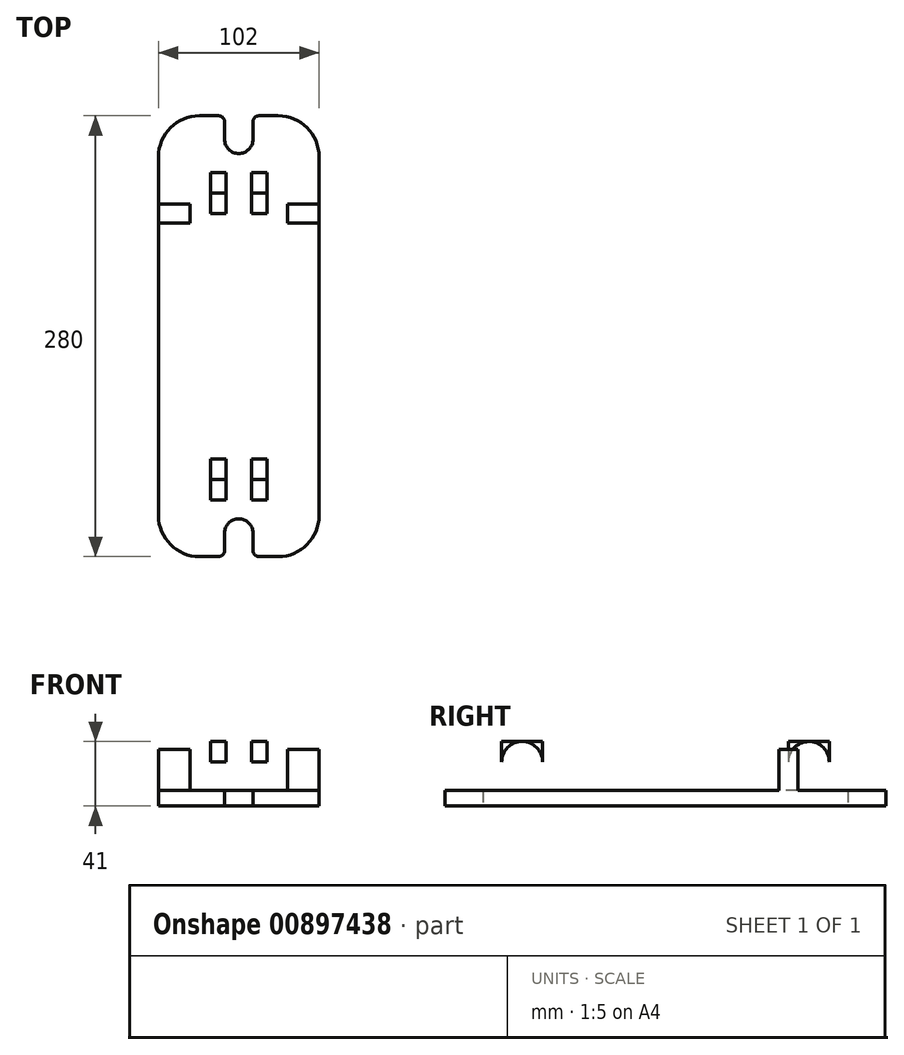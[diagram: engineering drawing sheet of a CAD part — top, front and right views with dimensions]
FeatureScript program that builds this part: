
annotation { "Feature Type Name" : "Feature", "Feature Type Description" : "" }
export const myFeature = defineFeature(function(context is Context, id is Id, definition is map)
    precondition{}
    {
        {
            var Q0;
            Q0=qCreatedBy(makeId("Top.planeOp"),FACE);
            var sketch = newSketch(context, id + "F0", { "sketchPlane" : qUnion([Q0])});
            skLineSegment(sketch, "E0.bottom", {"start": v(-25, 140) * mm, "end": v(-9, 140) * mm});
            skLineSegment(sketch, "E0.top", {"start": v(-25, -140) * mm, "end": v(-9, -140) * mm});
            skLineSegment(sketch, "E0.left", {"start": v(-51, 114) * mm, "end": v(-51, -114) * mm});
            skLineSegment(sketch, "E0.right", {"start": v(51, 114) * mm, "end": v(51, -114) * mm});
            skPoint(sketch, "E0.middle", {"position": v(0, 0) * mm});
            skLineSegment(sketch, "E1", {"start": v(9, -140) * mm, "end": v(9, -125) * mm});
            skPoint(sketch, "E2.startSnap0", {"position": v(0, -140) * mm});
            skLineSegment(sketch, "E3", {"start": v(0, -87.37) * mm, "end": v(0, 88.05) * mm, "construction": true});
            skLineSegment(sketch, "E4", {"start": v(90.42, 0) * mm, "end": v(-89.23, 0) * mm, "construction": true});
            skPoint(sketch, "E4.startSnap0", {"position": v(51, 0) * mm});
            skLineSegment(sketch, "E5.MirrorCS", {"start": v(-9, -140) * mm, "end": v(-9, -125) * mm});
            skPoint(sketch, "E6.MirrorCS.end.orphan", {"position": v(-9, -116) * mm});
            skLineSegment(sketch, "E7", {"start": v(0, -116) * mm, "end": v(0, -116) * mm});
            skPoint(sketch, "E8.visualSharp", {"position": v(9, -116) * mm});
            skArc(sketch, "E8.filletArc", {"start": v(9, -125) * mm, "mid": v(6.36, -118.64) * mm, "end": v(0, -116) * mm});
            skArc(sketch, "E9.filletArc", {"start": v(0, -116) * mm, "mid": v(-6.36, -118.64) * mm, "end": v(-9, -125) * mm});
            skLineSegment(sketch, "E10.trimOffspring", {"start": v(9, -140) * mm, "end": v(25, -140) * mm});
            skLineSegment(sketch, "E11.MirrorCS", {"start": v(9, 140) * mm, "end": v(9, 125) * mm});
            skArc(sketch, "E12.MirrorCS", {"start": v(9, 125) * mm, "mid": v(6.36, 118.64) * mm, "end": v(0, 116) * mm});
            skArc(sketch, "E13.MirrorCS", {"start": v(0, 116) * mm, "mid": v(-6.36, 118.64) * mm, "end": v(-9, 125) * mm});
            skLineSegment(sketch, "E14.MirrorCS", {"start": v(-9, 140) * mm, "end": v(-9, 125) * mm});
            skLineSegment(sketch, "E15.trimOffspring", {"start": v(9, 140) * mm, "end": v(25, 140) * mm});
            skPoint(sketch, "E16.visualSharp", {"position": v(51, 140) * mm});
            skArc(sketch, "E16.filletArc", {"start": v(51, 114) * mm, "mid": v(43.38, 132.38) * mm, "end": v(25, 140) * mm});
            skPoint(sketch, "E17.visualSharp", {"position": v(-51, 140) * mm});
            skArc(sketch, "E17.filletArc", {"start": v(-25, 140) * mm, "mid": v(-43.38, 132.38) * mm, "end": v(-51, 114) * mm});
            skPoint(sketch, "E18.visualSharp", {"position": v(-51, -140) * mm});
            skArc(sketch, "E18.filletArc", {"start": v(-51, -114) * mm, "mid": v(-43.38, -132.38) * mm, "end": v(-25, -140) * mm});
            skPoint(sketch, "E19.visualSharp", {"position": v(51, -140) * mm});
            skArc(sketch, "E19.filletArc", {"start": v(25, -140) * mm, "mid": v(43.38, -132.38) * mm, "end": v(51, -114) * mm});
            skSolve(sketch);
        }
        {
            var Q0;
            Q0=makeQuery(id+"F0.imprint","IMPRINT",FACE,{"disambiguationData":[TD([[makeQuery(id+"F0.imprint","IMPRINT",EDGE,{"derivedFrom":sQuery(id+"F0.wireOp",EDGE,"E0.bottom")}),-1.0]])]});
            extrude(context, id + "F1", {"entities" : qUnion([Q0]), "depth" : 10 * mm, "offsetDistance" : 25 * mm});
        }
        {
            var Q0;
            Q0=makeQuery(id+"F1.opExtrude","SWEPT_EDGE",EDGE,{"disambiguationData":[OSD([sQuery(id+"F0.wireOp",EDGE,"E0.top"),sQuery(id+"F0.wireOp",EDGE,"E5.MirrorCS")])]});
            var Q1;
            Q1=makeQuery(id+"F1.opExtrude","SWEPT_EDGE",EDGE,{"disambiguationData":[OSD([sQuery(id+"F0.wireOp",EDGE,"E1"),sQuery(id+"F0.wireOp",EDGE,"E10.trimOffspring")])]});
            var Q2;
            Q2=makeQuery(id+"F1.opExtrude","SWEPT_EDGE",EDGE,{"disambiguationData":[OSD([sQuery(id+"F0.wireOp",EDGE,"E0.bottom"),sQuery(id+"F0.wireOp",EDGE,"E14.MirrorCS")])]});
            var Q3;
            Q3=makeQuery(id+"F1.opExtrude","SWEPT_EDGE",EDGE,{"disambiguationData":[OSD([sQuery(id+"F0.wireOp",EDGE,"E11.MirrorCS"),sQuery(id+"F0.wireOp",EDGE,"E15.trimOffspring")])]});
            fillet(context, id + "F2", {"entities" : qUnion([Q0, Q1, Q2, Q3]), "radius" : 4 * mm, "tangentPropagation" : true, "allowEdgeOverflow" : false});
        }
        {
            var Q0;
            Q0=makeQuery(id+"F1.opExtrude","CAP_FACE",FACE,{"disambiguationData":[OSD([sQuery(id+"F0.wireOp",EDGE,"E0.bottom"),sQuery(id+"F0.wireOp",EDGE,"E0.top"),sQuery(id+"F0.wireOp",EDGE,"E0.left"),sQuery(id+"F0.wireOp",EDGE,"E0.right"),sQuery(id+"F0.wireOp",EDGE,"E1"),sQuery(id+"F0.wireOp",EDGE,"E5.MirrorCS"),sQuery(id+"F0.wireOp",EDGE,"E8.filletArc"),sQuery(id+"F0.wireOp",EDGE,"E9.filletArc"),sQuery(id+"F0.wireOp",EDGE,"E10.trimOffspring"),sQuery(id+"F0.wireOp",EDGE,"E11.MirrorCS"),sQuery(id+"F0.wireOp",EDGE,"E12.MirrorCS"),sQuery(id+"F0.wireOp",EDGE,"E13.MirrorCS"),sQuery(id+"F0.wireOp",EDGE,"E14.MirrorCS"),sQuery(id+"F0.wireOp",EDGE,"E15.trimOffspring"),sQuery(id+"F0.wireOp",EDGE,"E16.filletArc"),sQuery(id+"F0.wireOp",EDGE,"E17.filletArc"),sQuery(id+"F0.wireOp",EDGE,"E18.filletArc"),sQuery(id+"F0.wireOp",EDGE,"E19.filletArc")])],"isStart":false});
            var sketch = newSketch(context, id + "F3", { "sketchPlane" : qUnion([Q0])});
            skLineSegment(sketch, "E20", {"start": v(0, -153.2) * mm, "end": v(0, 125) * mm, "construction": true});
            skLineSegment(sketch, "E21", {"start": v(85.13, 0) * mm, "end": v(-87.5, 0) * mm, "construction": true});
            skPoint(sketch, "E21.endSnap0", {"position": v(51, 0) * mm});
            skLineSegment(sketch, "E22", {"start": v(8, -104) * mm, "end": v(18, -104) * mm});
            skLineSegment(sketch, "E23", {"start": v(8, -104) * mm, "end": v(8, -78) * mm});
            skLineSegment(sketch, "E24", {"start": v(8, -78) * mm, "end": v(18, -78) * mm});
            skLineSegment(sketch, "E25", {"start": v(18, -78) * mm, "end": v(18, -104) * mm});
            skLineSegment(sketch, "E26.MirrorCS", {"start": v(-8, -104) * mm, "end": v(-8, -78) * mm});
            skLineSegment(sketch, "E27.MirrorCS", {"start": v(-8, -78) * mm, "end": v(-18, -78) * mm});
            skLineSegment(sketch, "E28.MirrorCS", {"start": v(-18, -78) * mm, "end": v(-18, -104) * mm});
            skLineSegment(sketch, "E29.MirrorCS", {"start": v(-8, -104) * mm, "end": v(-18, -104) * mm});
            skLineSegment(sketch, "E30.MirrorCS", {"start": v(-18, 78) * mm, "end": v(-18, 104) * mm});
            skLineSegment(sketch, "E31.MirrorCS", {"start": v(-8, 78) * mm, "end": v(-18, 78) * mm});
            skLineSegment(sketch, "E32.MirrorCS", {"start": v(-8, 104) * mm, "end": v(-8, 78) * mm});
            skLineSegment(sketch, "E33.MirrorCS", {"start": v(-8, 104) * mm, "end": v(-18, 104) * mm});
            skLineSegment(sketch, "E34.MirrorCS", {"start": v(8, 104) * mm, "end": v(8, 78) * mm});
            skLineSegment(sketch, "E35.MirrorCS", {"start": v(8, 78) * mm, "end": v(18, 78) * mm});
            skLineSegment(sketch, "E36.MirrorCS", {"start": v(18, 78) * mm, "end": v(18, 104) * mm});
            skLineSegment(sketch, "E37.MirrorCS", {"start": v(8, 104) * mm, "end": v(18, 104) * mm});
            skSolve(sketch);
        }
        {
            var Q0;
            Q0 = qSketchRegion(id + "F3", true);
            extrude(context, id + "F4", {"entities" : qUnion([Q0]), "operationType" : NewBodyOperationType.ADD, "depth" : 31 * mm, "offsetDistance" : 25 * mm});
        }
        {
            var Q0;
            Q0=makeQuery(id+"F4.opExtrude","SWEPT_FACE",FACE,{"disambiguationData":[OSD([sQuery(id+"F3.wireOp",EDGE,"E25")])]});
            var sketch = newSketch(context, id + "F5", { "sketchPlane" : qUnion([Q0])});
            skLineSegment(sketch, "E38", {"start": v(-98.26, 28) * mm, "end": v(-80.47, 28) * mm, "construction": true});
            skLineSegment(sketch, "E39", {"start": v(-91, 17.94) * mm, "end": v(-91, 37.74) * mm, "construction": true});
            skPoint(sketch, "E39.startSnap0", {"position": v(-91, 10) * mm});
            skCircle(sketch, "E40", {"center": v(-91, 28) * mm, "radius": 6.5 * mm});
            skArc(sketch, "E41", {"start": v(-104, 28) * mm, "mid": v(-91, 41) * mm, "end": v(-78, 28) * mm});
            skSolve(sketch);
        }
        {
            var Q0;
            Q0=makeQuery(id+"F5.imprint","IMPRINT",FACE,{"disambiguationData":[TD([[makeQuery(id+"F5.imprint","IMPRINT",EDGE,{"derivedFrom":sQuery(id+"F5.wireOp",EDGE,"E40")}),1.0]])]});
            var Q1;
            {var subQ0=sQuery(id+"F5.wireOp",EDGE,"E41");var subQ1=sQuery(id+"F3.wireOp",EDGE,"E25");var subQ4=makeQuery(id+"F4.opExtrude","CAP_EDGE",EDGE,{"disambiguationData":[OSD([subQ1])],"isStart":false});var subQ5=makeQuery(id+"F5.imprint","INTERSECT",VERTEX,{"derivedFrom":[subQ4,subQ0]});Q1=makeQuery(id+"F5.imprint","IMPRINT",FACE,{"disambiguationData":[TD([[makeQuery(id+"F5.imprint","IMPRINT",EDGE,{"disambiguationData":[TD([[subQ5,1.0]])],"derivedFrom":subQ0}),1.0]])]});}
            var Q2;
            {var subQ0=sQuery(id+"F5.wireOp",EDGE,"E41");var subQ1=sQuery(id+"F3.wireOp",EDGE,"E25");var subQ4=makeQuery(id+"F4.opExtrude","CAP_EDGE",EDGE,{"disambiguationData":[OSD([subQ1])],"isStart":false});var subQ5=makeQuery(id+"F5.imprint","INTERSECT",VERTEX,{"derivedFrom":[subQ4,subQ0]});Q2=makeQuery(id+"F5.imprint","IMPRINT",FACE,{"disambiguationData":[TD([[makeQuery(id+"F5.imprint","IMPRINT",EDGE,{"disambiguationData":[TD([[subQ5,-1.0]])],"derivedFrom":subQ0}),1.0]])]});}
            extrude(context, id + "F6", {"entities" : qUnion([Q0, Q1, Q2]), "operationType" : NewBodyOperationType.REMOVE, "endBound" : BoundingType.THROUGH_ALL, "oppositeDirection" : true, "depth" : 25 * mm, "offsetDistance" : 25 * mm});
        }
        {
            var Q0;
            Q0=makeQuery(id+"F4.opExtrude","SWEPT_FACE",FACE,{"disambiguationData":[OSD([sQuery(id+"F3.wireOp",EDGE,"E36.MirrorCS")])]});
            var sketch = newSketch(context, id + "F7", { "sketchPlane" : qUnion([Q0])});
            skLineSegment(sketch, "E42", {"start": v(80.32, 28) * mm, "end": v(100.5, 28) * mm, "construction": true});
            skLineSegment(sketch, "E43", {"start": v(91, 10) * mm, "end": v(91, 33.92) * mm, "construction": true});
            skCircle(sketch, "E44", {"center": v(91, 28) * mm, "radius": 6.5 * mm});
            skArc(sketch, "E45", {"start": v(78, 28) * mm, "mid": v(91, 41) * mm, "end": v(104, 28) * mm});
            skSolve(sketch);
        }
        {
            var Q0;
            Q0=makeQuery(id+"F7.imprint","IMPRINT",FACE,{"disambiguationData":[TD([[makeQuery(id+"F7.imprint","IMPRINT",EDGE,{"derivedFrom":sQuery(id+"F7.wireOp",EDGE,"E44")}),1.0]])]});
            var Q1;
            {var subQ0=sQuery(id+"F7.wireOp",EDGE,"E45");var subQ1=sQuery(id+"F3.wireOp",EDGE,"E36.MirrorCS");var subQ4=makeQuery(id+"F4.opExtrude","CAP_EDGE",EDGE,{"disambiguationData":[OSD([subQ1])],"isStart":false});var subQ5=makeQuery(id+"F7.imprint","INTERSECT",VERTEX,{"derivedFrom":[subQ4,subQ0]});Q1=makeQuery(id+"F7.imprint","IMPRINT",FACE,{"disambiguationData":[TD([[makeQuery(id+"F7.imprint","IMPRINT",EDGE,{"disambiguationData":[TD([[subQ5,-1.0]])],"derivedFrom":subQ0}),1.0]])]});}
            var Q2;
            {var subQ0=sQuery(id+"F7.wireOp",EDGE,"E45");var subQ1=sQuery(id+"F3.wireOp",EDGE,"E36.MirrorCS");var subQ4=makeQuery(id+"F4.opExtrude","CAP_EDGE",EDGE,{"disambiguationData":[OSD([subQ1])],"isStart":false});var subQ5=makeQuery(id+"F7.imprint","INTERSECT",VERTEX,{"derivedFrom":[subQ4,subQ0]});Q2=makeQuery(id+"F7.imprint","IMPRINT",FACE,{"disambiguationData":[TD([[makeQuery(id+"F7.imprint","IMPRINT",EDGE,{"disambiguationData":[TD([[subQ5,1.0]])],"derivedFrom":subQ0}),1.0]])]});}
            extrude(context, id + "F8", {"entities" : qUnion([Q0, Q1, Q2]), "operationType" : NewBodyOperationType.REMOVE, "endBound" : BoundingType.THROUGH_ALL, "oppositeDirection" : true, "depth" : 25 * mm, "offsetDistance" : 25 * mm});
        }
        {
            var Q0;
            Q0=makeQuery(id+"F1.opExtrude","CAP_FACE",FACE,{"disambiguationData":[OSD([sQuery(id+"F0.wireOp",EDGE,"E0.bottom"),sQuery(id+"F0.wireOp",EDGE,"E0.top"),sQuery(id+"F0.wireOp",EDGE,"E0.left"),sQuery(id+"F0.wireOp",EDGE,"E0.right"),sQuery(id+"F0.wireOp",EDGE,"E1"),sQuery(id+"F0.wireOp",EDGE,"E5.MirrorCS"),sQuery(id+"F0.wireOp",EDGE,"E8.filletArc"),sQuery(id+"F0.wireOp",EDGE,"E9.filletArc"),sQuery(id+"F0.wireOp",EDGE,"E10.trimOffspring"),sQuery(id+"F0.wireOp",EDGE,"E11.MirrorCS"),sQuery(id+"F0.wireOp",EDGE,"E12.MirrorCS"),sQuery(id+"F0.wireOp",EDGE,"E13.MirrorCS"),sQuery(id+"F0.wireOp",EDGE,"E14.MirrorCS"),sQuery(id+"F0.wireOp",EDGE,"E15.trimOffspring"),sQuery(id+"F0.wireOp",EDGE,"E16.filletArc"),sQuery(id+"F0.wireOp",EDGE,"E17.filletArc"),sQuery(id+"F0.wireOp",EDGE,"E18.filletArc"),sQuery(id+"F0.wireOp",EDGE,"E19.filletArc")])],"isStart":false});
            var sketch = newSketch(context, id + "F9", { "sketchPlane" : qUnion([Q0])});
            skLineSegment(sketch, "E46", {"start": v(51, 84) * mm, "end": v(31, 84) * mm});
            skLineSegment(sketch, "E47", {"start": v(31, 84) * mm, "end": v(31, 72) * mm});
            skLineSegment(sketch, "E48", {"start": v(31, 72) * mm, "end": v(51, 72) * mm});
            skLineSegment(sketch, "E49", {"start": v(51, 72) * mm, "end": v(51, 84) * mm});
            skLineSegment(sketch, "E50", {"start": v(0, 0) * mm, "end": v(63.4, 0) * mm, "construction": true});
            skLineSegment(sketch, "E51", {"start": v(0, -23.09) * mm, "end": v(0, 131.02) * mm, "construction": true});
            skLineSegment(sketch, "E52.MirrorCS", {"start": v(-31, 84) * mm, "end": v(-31, 72) * mm});
            skLineSegment(sketch, "E53.MirrorCS", {"start": v(-51, 84) * mm, "end": v(-31, 84) * mm});
            skLineSegment(sketch, "E54.MirrorCS", {"start": v(-51, 72) * mm, "end": v(-51, 84) * mm});
            skLineSegment(sketch, "E55.MirrorCS", {"start": v(-31, 72) * mm, "end": v(-51, 72) * mm});
            skSolve(sketch);
        }
        {
            var Q0;
            Q0=makeQuery(id+"F9.imprint","IMPRINT",FACE,{"disambiguationData":[TD([[makeQuery(id+"F9.imprint","IMPRINT",EDGE,{"derivedFrom":sQuery(id+"F9.wireOp",EDGE,"E46")}),1.0]])]});
            var Q1;
            Q1=makeQuery(id+"F9.imprint","IMPRINT",FACE,{"disambiguationData":[TD([[makeQuery(id+"F9.imprint","IMPRINT",EDGE,{"derivedFrom":sQuery(id+"F9.wireOp",EDGE,"E52.MirrorCS")}),-1.0]])]});
            extrude(context, id + "F10", {"entities" : qUnion([Q0, Q1]), "operationType" : NewBodyOperationType.ADD, "depth" : 26 * mm, "offsetDistance" : 25 * mm});
        }
    });
